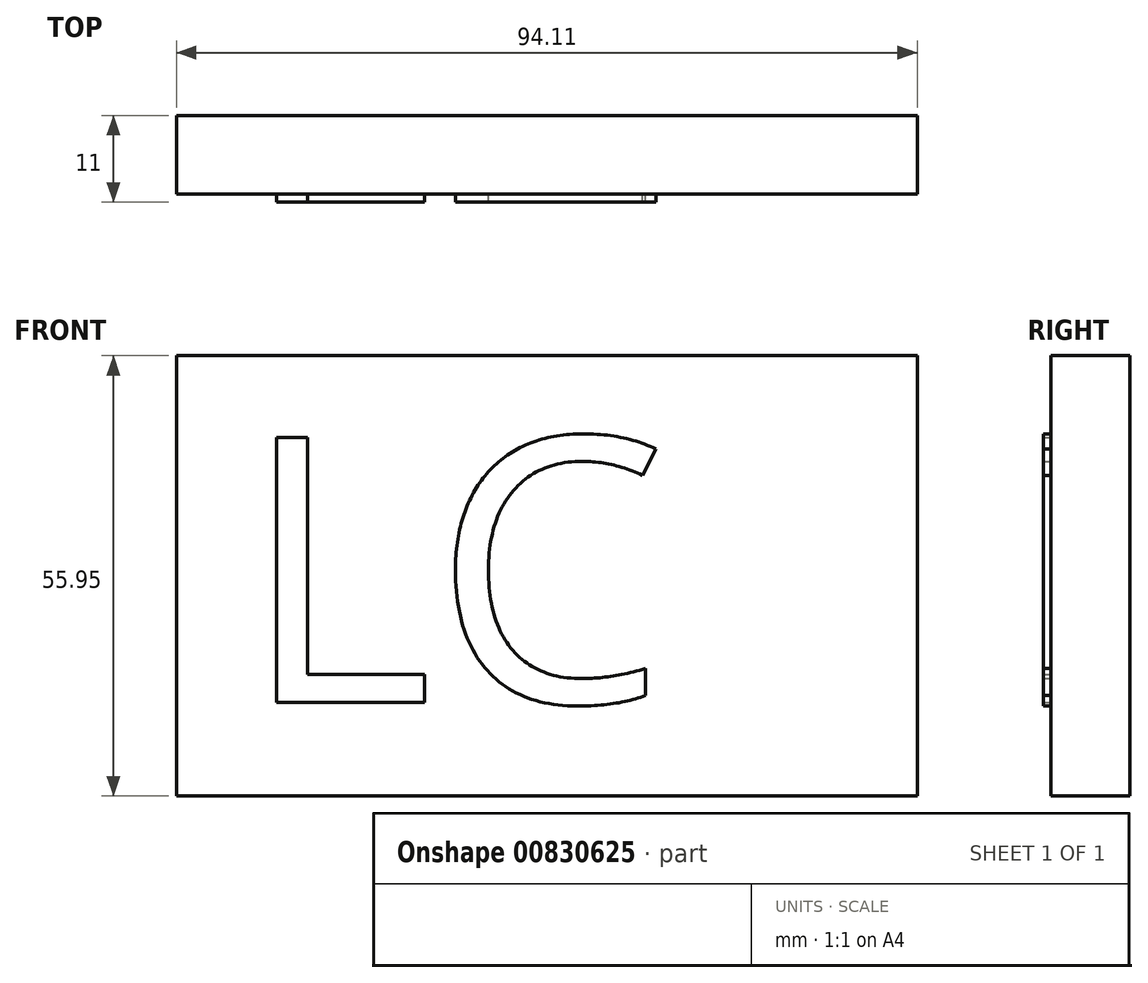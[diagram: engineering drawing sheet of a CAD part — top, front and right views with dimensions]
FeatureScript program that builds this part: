
annotation { "Feature Type Name" : "Feature", "Feature Type Description" : "" }
export const myFeature = defineFeature(function(context is Context, id is Id, definition is map)
    precondition{}
    {
        {
            var Q0;
            Q0=qCreatedBy(makeId("Front.planeOp"),FACE);
            var sketch = newSketch(context, id + "F0", { "sketchPlane" : qUnion([Q0])});
            skLineSegment(sketch, "E0.bottom", {"start": v(0, 0) * mm, "end": v(94.11, 0) * mm});
            skLineSegment(sketch, "E0.top", {"start": v(0, 55.95) * mm, "end": v(94.11, 55.95) * mm});
            skLineSegment(sketch, "E0.left", {"start": v(0, 0) * mm, "end": v(0, 55.95) * mm});
            skLineSegment(sketch, "E0.right", {"start": v(94.11, 0) * mm, "end": v(94.11, 55.95) * mm});
            skSolve(sketch);
        }
        {
            var Q0;
            Q0=makeQuery(id+"F0.imprint","IMPRINT",FACE,{"disambiguationData":[TD([[makeQuery(id+"F0.imprint","IMPRINT",EDGE,{"derivedFrom":sQuery(id+"F0.wireOp",EDGE,"E0.bottom")}),1.0]])]});
            extrude(context, id + "F1", {"entities" : qUnion([Q0]), "depth" : 10 * mm, "offsetDistance" : 25.4 * mm});
        }
        {
            var Q0;
            Q0=makeQuery(id+"F1.opExtrude","CAP_FACE",FACE,{"disambiguationData":[OSD([sQuery(id+"F0.wireOp",EDGE,"E0.bottom"),sQuery(id+"F0.wireOp",EDGE,"E0.top"),sQuery(id+"F0.wireOp",EDGE,"E0.left"),sQuery(id+"F0.wireOp",EDGE,"E0.right")])],"isStart":false});
            var sketch = newSketch(context, id + "F2", { "sketchPlane" : qUnion([Q0])});
            skText(sketch, "E1", { "text": "LC", "fontName": "OpenSans-Regular.ttf"});
            const initialGuessF2  = {"E1": [0.00812, 0.0119, 1, 0, 0.03392]};
            skSetInitialGuess(sketch, initialGuessF2);
            skSolve(sketch);
        }
        {
            var Q0;
            Q0 = qSketchRegion(id + "F2", true);
            extrude(context, id + "F3", {"entities" : qUnion([Q0]), "operationType" : NewBodyOperationType.ADD, "depth" : 1 * mm, "offsetDistance" : 25.4 * mm});
        }
    });
